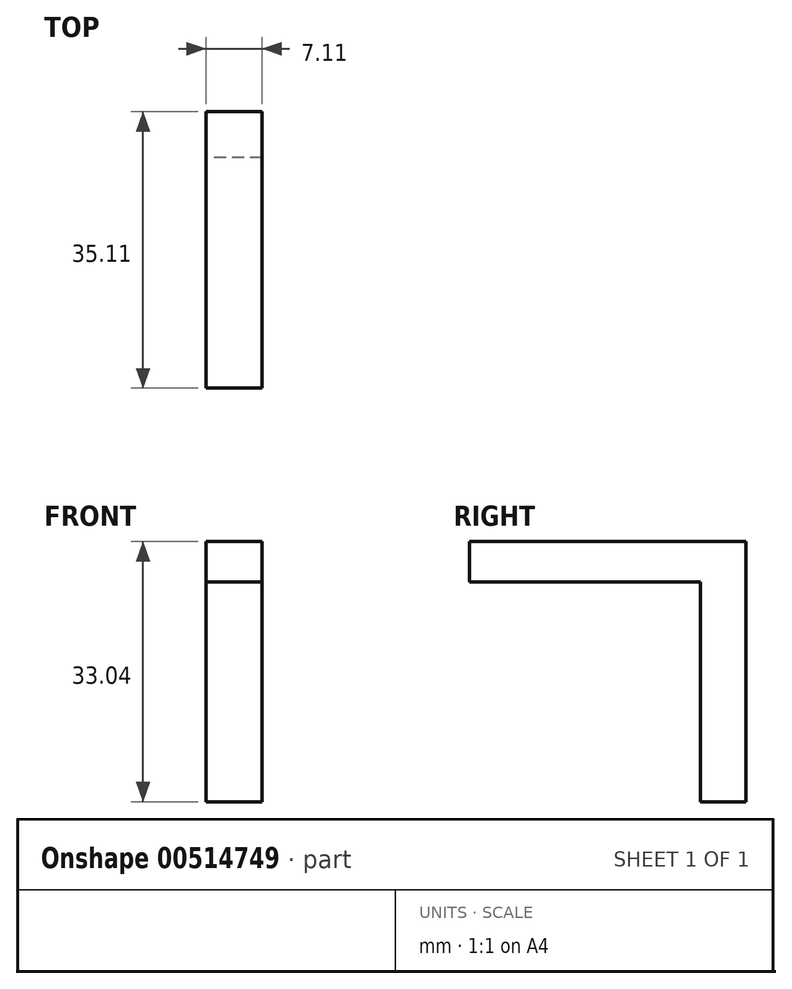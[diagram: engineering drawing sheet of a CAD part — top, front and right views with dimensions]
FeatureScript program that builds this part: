
annotation { "Feature Type Name" : "Feature", "Feature Type Description" : "" }
export const myFeature = defineFeature(function(context is Context, id is Id, definition is map)
    precondition{}
    {
        {
            var Q0;
            Q0=qCreatedBy(makeId("Right.planeOp"),FACE);
            var sketch = newSketch(context, id + "F0", { "sketchPlane" : qUnion([Q0])});
            skLineSegment(sketch, "E0.bottom", {"start": v(-35.11, 38.44) * mm, "end": v(0, 38.44) * mm});
            skLineSegment(sketch, "E0.top", {"start": v(-35.11, 33.36) * mm, "end": v(0, 33.36) * mm});
            skLineSegment(sketch, "E0.left", {"start": v(-35.11, 38.44) * mm, "end": v(-35.11, 33.36) * mm});
            skLineSegment(sketch, "E0.right", {"start": v(0, 38.44) * mm, "end": v(0, 33.36) * mm});
            skLineSegment(sketch, "E1.bottom", {"start": v(0, 38.44) * mm, "end": v(-5.84, 38.44) * mm});
            skLineSegment(sketch, "E1.top", {"start": v(0, 5.4) * mm, "end": v(-5.84, 5.4) * mm});
            skLineSegment(sketch, "E1.left", {"start": v(0, 38.44) * mm, "end": v(0, 5.4) * mm});
            skLineSegment(sketch, "E1.right", {"start": v(-5.84, 38.44) * mm, "end": v(-5.84, 5.4) * mm});
            skSolve(sketch);
        }
        {
            var Q0;
            Q0 = qSketchRegion(id + "F0", true);
            extrude(context, id + "F1", {"entities" : qUnion([Q0]), "depth" : 7.11 * mm, "offsetDistance" : 25.4 * mm});
        }
    });
